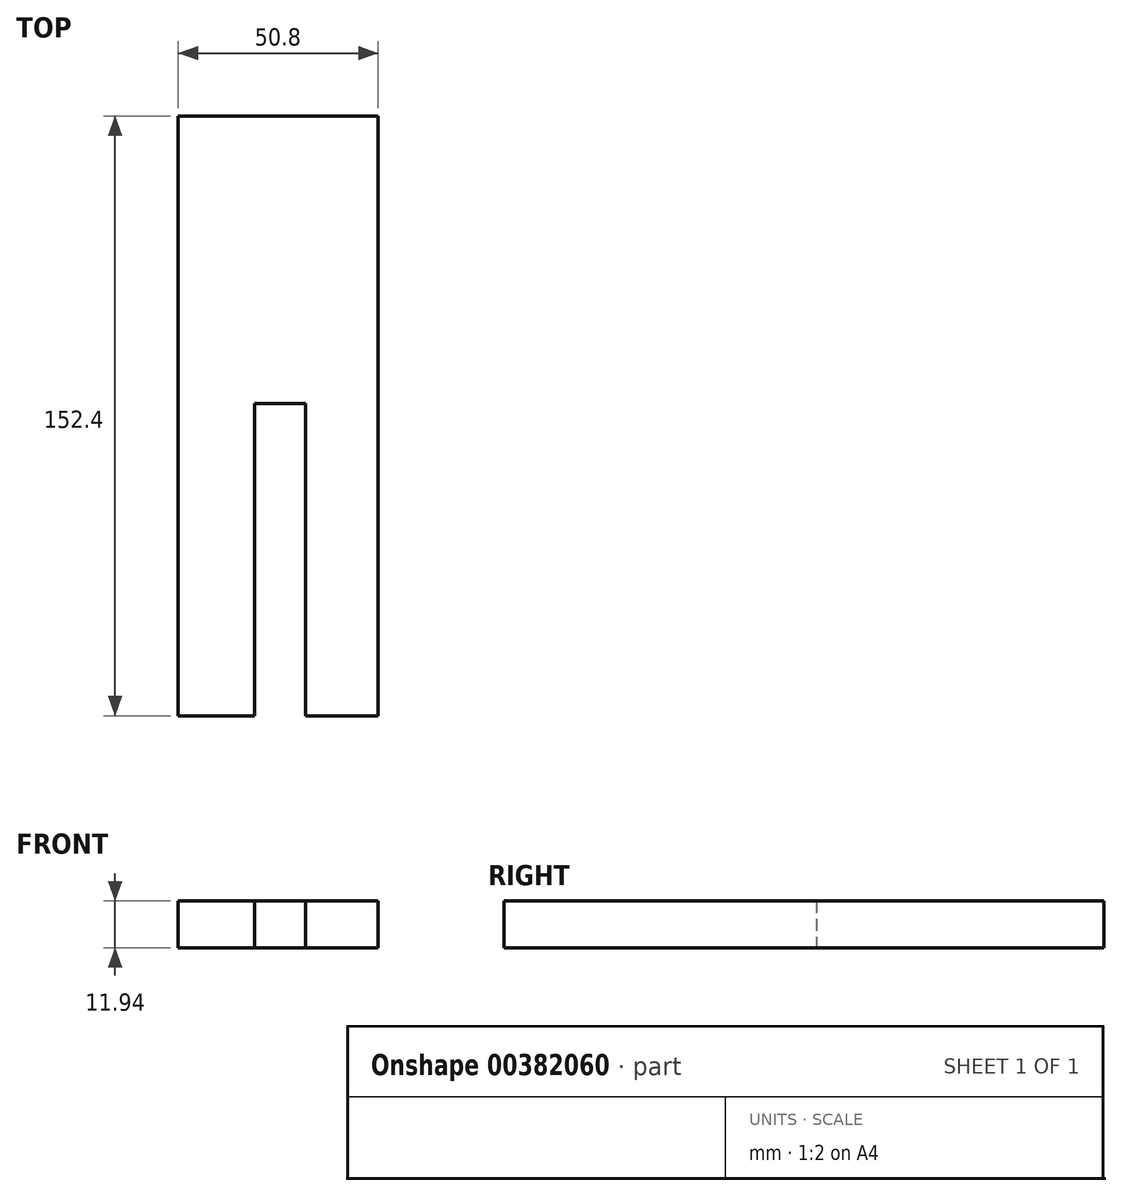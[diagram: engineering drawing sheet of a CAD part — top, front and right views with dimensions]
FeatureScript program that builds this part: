
annotation { "Feature Type Name" : "Feature", "Feature Type Description" : "" }
export const myFeature = defineFeature(function(context is Context, id is Id, definition is map)
    precondition{}
    {
        {
            var Q0;
            Q0=qCreatedBy(makeId("Top.planeOp"),FACE);
            var sketch = newSketch(context, id + "F0", { "sketchPlane" : qUnion([Q0])});
            skLineSegment(sketch, "E0.bottom", {"start": v(-23.42, 0) * mm, "end": v(-4, 0) * mm});
            skLineSegment(sketch, "E0.top", {"start": v(-23.42, 152.4) * mm, "end": v(27.38, 152.4) * mm});
            skLineSegment(sketch, "E0.left", {"start": v(-23.42, 0) * mm, "end": v(-23.42, 152.4) * mm});
            skLineSegment(sketch, "E0.right", {"start": v(27.38, 0) * mm, "end": v(27.38, 152.4) * mm});
            skLineSegment(sketch, "E1", {"start": v(-4, 0) * mm, "end": v(-4, 76.2) * mm});
            skLineSegment(sketch, "E2", {"start": v(8.95, 76.2) * mm, "end": v(8.95, 0) * mm});
            skLineSegment(sketch, "E3.trimOffspring", {"start": v(8.95, 0) * mm, "end": v(27.38, 0) * mm});
            skLineSegment(sketch, "E4", {"start": v(8.95, 76.2) * mm, "end": v(8.95, 79.38) * mm});
            skLineSegment(sketch, "E5", {"start": v(8.95, 79.38) * mm, "end": v(-4, 79.38) * mm});
            skLineSegment(sketch, "E6", {"start": v(-4, 76.2) * mm, "end": v(-4, 79.38) * mm});
            skPoint(sketch, "E7", {"position": v(-4, 76.2) * mm});
            skPoint(sketch, "E8", {"position": v(8.95, 76.2) * mm});
            skLineSegment(sketch, "E9", {"start": v(8.95, 76.2) * mm, "end": v(-4, 76.2) * mm, "construction": true});
            skSolve(sketch);
        }
        {
            var Q0;
            Q0=makeQuery(id+"F0.imprint","IMPRINT",FACE,{"disambiguationData":[TD([[makeQuery(id+"F0.imprint","IMPRINT",EDGE,{"derivedFrom":sQuery(id+"F0.wireOp",EDGE,"E0.bottom")}),1.0]])]});
            extrude(context, id + "F1", {"entities" : qUnion([Q0]), "depth" : 11.94 * mm});
        }
    });
